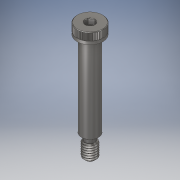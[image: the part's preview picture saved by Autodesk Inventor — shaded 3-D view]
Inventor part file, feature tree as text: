
AUTODESK INVENTOR PART (.ipt)
format: ipt  version: 2017 (Build 210142000, 142)  size: 585,728 bytes
history: native  units: in
note: dims shown in document units (in); Inventor stores cm internally (conversion verified against a paired STEP export)
features: chamfer x1
ambient origin geometry x8: Origin, YZ Plane, XZ Plane, XY Plane, X Axis, Y Axis, Z Axis, Center Point
bodies: Solid1 (feature_tree)
feature tree (1):
  chamfer  "Chamfer3"  [1 undecoded]
note: 1 required parameter value undecoded (feature->parameter linkage not recoverable at this tier; creation-order binding heuristic only, values carry confidence <= 0.55)
